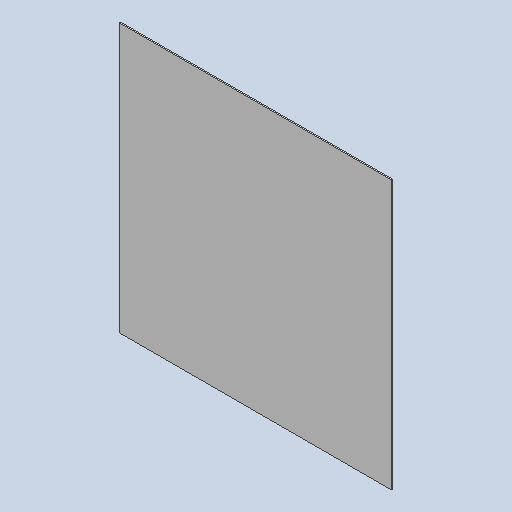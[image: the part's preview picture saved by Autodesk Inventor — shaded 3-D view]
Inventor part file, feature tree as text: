
AUTODESK INVENTOR PART (.ipt)
format: ipt  version: 2025 (Build 290162010, 162A)  size: 105,472 bytes
history: native  units: mm
features: extrude x1, other x1
ambient origin geometry x8: Origin, YZ Plane, XZ Plane, XY Plane, X Axis, Y Axis, Z Axis, Center Point
bodies: Solid1 (feature_tree)
feature tree (2):
  extrude  "Extrusion1"  Depth=2180.0mm
  other  "Definition1"
